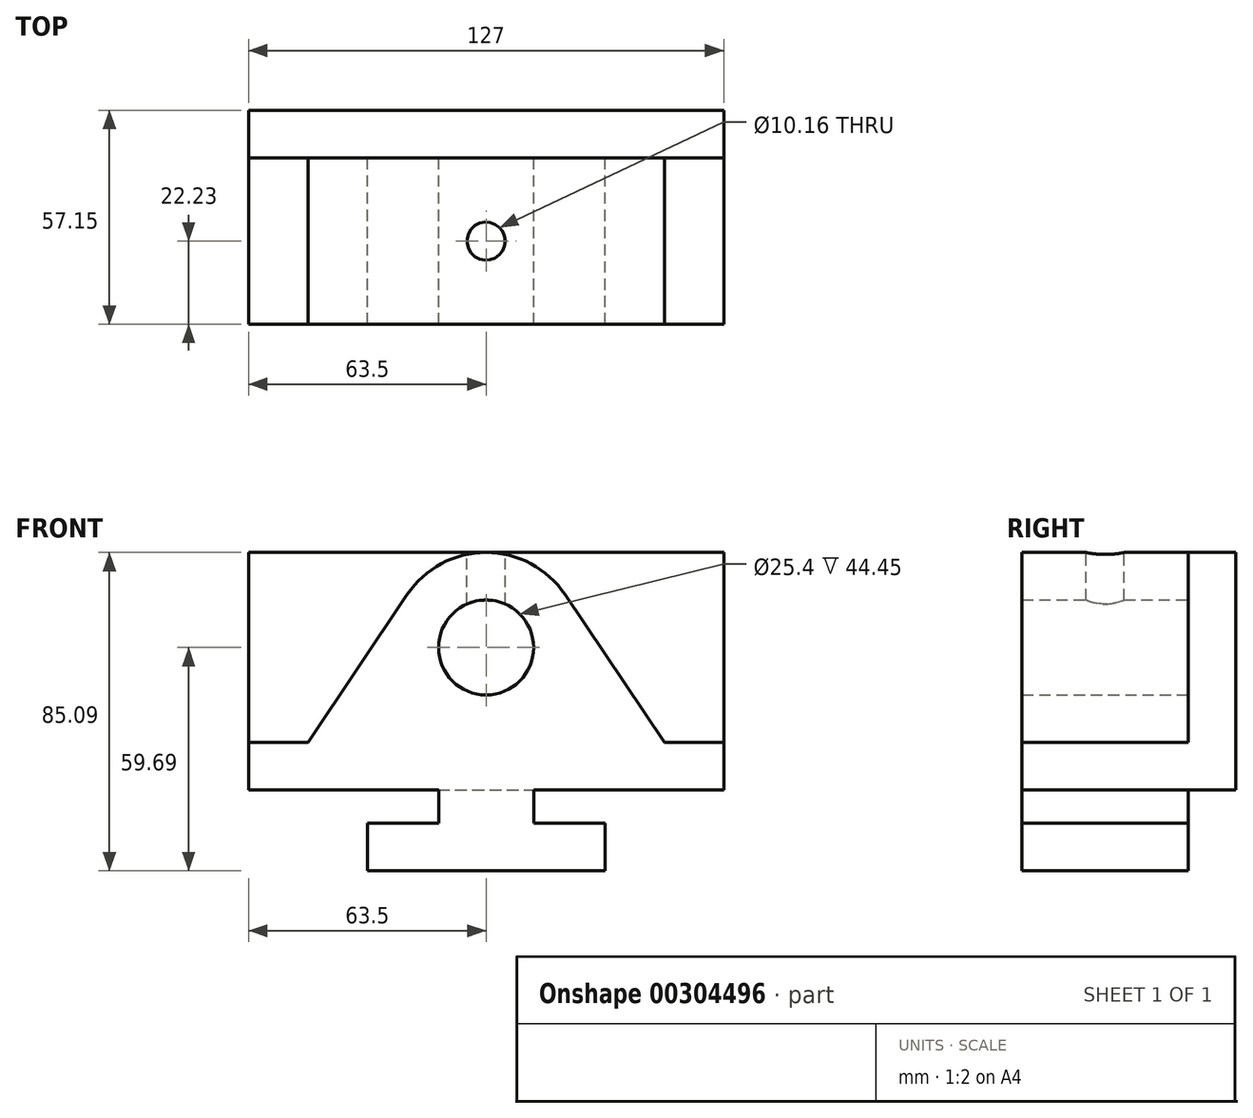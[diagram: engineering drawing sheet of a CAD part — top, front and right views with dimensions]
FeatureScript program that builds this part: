
annotation { "Feature Type Name" : "Feature", "Feature Type Description" : "" }
export const myFeature = defineFeature(function(context is Context, id is Id, definition is map)
    precondition{}
    {
        {
            var Q0;
            Q0=qCreatedBy(makeId("Front.planeOp"),FACE);
            var sketch = newSketch(context, id + "F0", { "sketchPlane" : qUnion([Q0])});
            skLineSegment(sketch, "E0.bottom", {"start": v(-31.75, -21.6) * mm, "end": v(-12.7, -21.6) * mm});
            skLineSegment(sketch, "E0.top", {"start": v(-31.75, -34.3) * mm, "end": v(31.75, -34.29) * mm});
            skLineSegment(sketch, "E0.left", {"start": v(-31.75, -21.59) * mm, "end": v(-31.75, -34.3) * mm});
            skLineSegment(sketch, "E0.right", {"start": v(31.75, -21.59) * mm, "end": v(31.75, -34.3) * mm});
            skLineSegment(sketch, "E1.left", {"start": v(-12.7, -21.6) * mm, "end": v(-12.7, -12.7) * mm});
            skLineSegment(sketch, "E1.right", {"start": v(12.7, -21.6) * mm, "end": v(12.7, -12.7) * mm});
            skLineSegment(sketch, "E2.bottom", {"start": v(-63.5, 0) * mm, "end": v(-47.63, 0) * mm});
            skLineSegment(sketch, "E2.top", {"start": v(-63.5, -12.7) * mm, "end": v(-12.7, -12.7) * mm});
            skLineSegment(sketch, "E2.left", {"start": v(-63.5, 0) * mm, "end": v(-63.5, -12.7) * mm});
            skLineSegment(sketch, "E2.right", {"start": v(63.5, 0) * mm, "end": v(63.5, -12.7) * mm});
            skLineSegment(sketch, "E3.trimOffspring", {"start": v(12.7, -12.7) * mm, "end": v(63.5, -12.7) * mm});
            skLineSegment(sketch, "E4.trimOffspring", {"start": v(12.7, -21.59) * mm, "end": v(31.75, -21.59) * mm});
            skLineSegment(sketch, "E5", {"start": v(-47.63, 0) * mm, "end": v(-21.1, 39.55) * mm});
            skLineSegment(sketch, "E6.MirrorCS", {"start": v(47.62, 0) * mm, "end": v(21.1, 39.55) * mm});
            skPoint(sketch, "E7.visualSharp", {"position": v(0, 71) * mm});
            skArc(sketch, "E7.filletArc", {"start": v(21.1, 39.55) * mm, "mid": v(0, 50.8) * mm, "end": v(-21.1, 39.55) * mm});
            skLineSegment(sketch, "E8.trimOffspring", {"start": v(47.63, 0) * mm, "end": v(63.5, 0) * mm});
            skLineSegment(sketch, "E9", {"start": v(-63.5, 0) * mm, "end": v(63.5, 0) * mm, "construction": true});
            skCircle(sketch, "E10", {"center": v(0, 25.4) * mm, "radius": 12.7 * mm});
            skSolve(sketch);
        }
        {
            var Q0;
            Q0 = qSketchRegion(id + "F0", true);
            extrude(context, id + "F1", {"entities" : qUnion([Q0]), "endBound" : BoundingType.SYMMETRIC, "depth" : 44.45 * mm});
        }
        {
            var Q0;
            Q0=makeQuery(id+"F1.opExtrude","SWEPT_FACE",FACE,{"disambiguationData":[OSD([sQuery(id+"F0.wireOp",EDGE,"E2.right")])]});
            var sketch = newSketch(context, id + "F2", { "sketchPlane" : qUnion([Q0])});
            skLineSegment(sketch, "E11.bottom", {"start": v(22.23, -12.7) * mm, "end": v(34.92, -12.7) * mm});
            skLineSegment(sketch, "E11.top", {"start": v(22.23, 50.8) * mm, "end": v(34.92, 50.8) * mm});
            skLineSegment(sketch, "E11.left", {"start": v(22.23, -12.7) * mm, "end": v(22.23, 50.8) * mm});
            skLineSegment(sketch, "E11.right", {"start": v(34.93, -12.7) * mm, "end": v(34.92, 50.8) * mm});
            skSolve(sketch);
        }
        {
            var Q0;
            Q0 = qSketchRegion(id + "F2", true);
            extrude(context, id + "F3", {"entities" : qUnion([Q0]), "operationType" : NewBodyOperationType.ADD, "oppositeDirection" : true, "depth" : 127 * mm});
        }
        {
            var Q0;
            Q0=makeQuery(id+"F3.opExtrude","SWEPT_FACE",FACE,{"disambiguationData":[OSD([sQuery(id+"F2.wireOp",EDGE,"E11.top")])]});
            var sketch = newSketch(context, id + "F4", { "sketchPlane" : qUnion([Q0])});
            skCircle(sketch, "E12", {"center": v(0, 0) * mm, "radius": 5.08 * mm});
            skSolve(sketch);
        }
        {
            var Q0;
            Q0 = qSketchRegion(id + "F4", true);
            extrude(context, id + "F5", {"entities" : qUnion([Q0]), "operationType" : NewBodyOperationType.REMOVE, "endBound" : BoundingType.UP_TO_NEXT, "oppositeDirection" : true, "depth" : 25.4 * mm});
        }
    });
